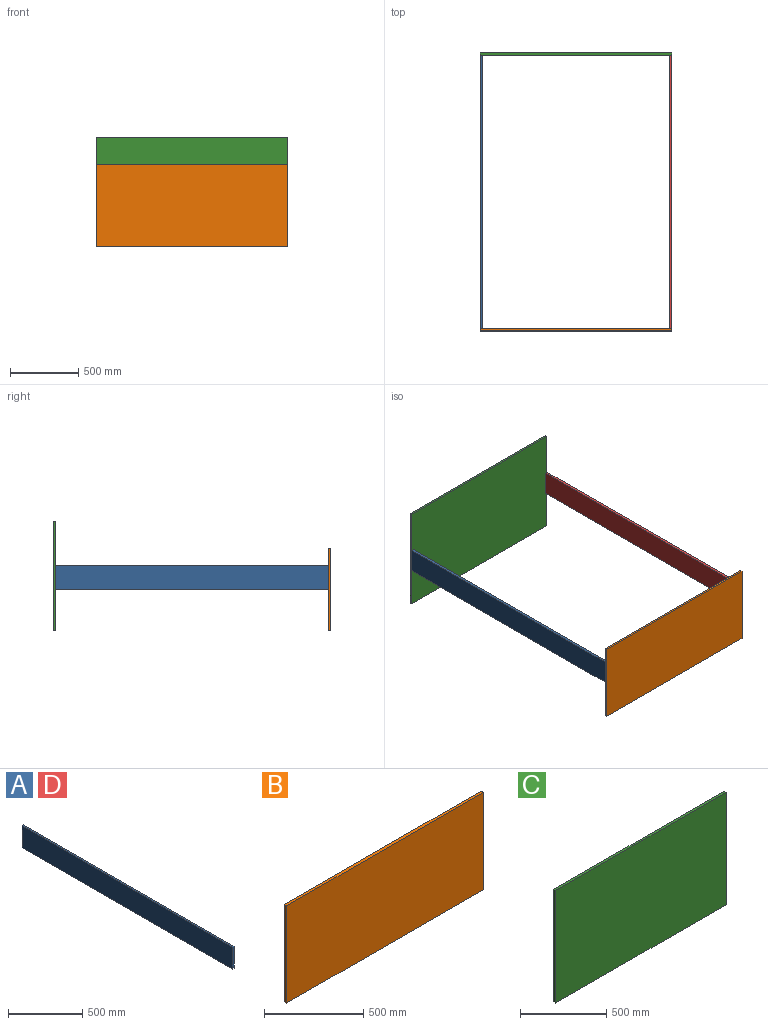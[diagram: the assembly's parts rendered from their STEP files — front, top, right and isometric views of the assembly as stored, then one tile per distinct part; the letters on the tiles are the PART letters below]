
ASSEMBLY  parts=4 mates=3
PART A: 6 faces, bbox 16x2000x180 mm
  f0: plane 2000x16mm, normal (0,0,1), area 32000mm2, adj f1,f3,f4,f5
  f1: plane 180x16mm, normal (0,-1,0), area 2880mm2, adj f0,f2,f4,f5
  f2: plane 2000x16mm, normal (0,0,-1), area 32000mm2, adj f1,f3,f4,f5
  f3: plane 180x16mm, normal (0,1,0), area 2880mm2, adj f0,f2,f4,f5
  f4: plane 2000x180mm, normal (1,0,0), area 360000mm2, adj f0,f1,f2,f3
  f5: plane 2000x180mm, normal (-1,0,0), area 360000mm2, adj f0,f1,f2,f3
PART B: 6 faces, bbox 1400x16x600 mm
  f0: plane 600x16mm, normal (1,0,0), area 9600mm2, adj f1,f3,f4,f5
  f1: plane 1400x16mm, normal (0,0,1), area 22400mm2, adj f0,f2,f4,f5
  f2: plane 600x16mm, normal (-1,0,0), area 9600mm2, adj f1,f3,f4,f5
  f3: plane 1400x16mm, normal (0,0,-1), area 22400mm2, adj f0,f2,f4,f5
  f4: plane 1400x600mm, normal (0,-1,0), area 840000mm2, adj f0,f1,f2,f3
  f5: plane 1400x600mm, normal (0,1,0), area 840000mm2, adj f0,f1,f2,f3
PART C: 6 faces, bbox 1400x16x800 mm
  f0: plane 800x16mm, normal (1,0,0), area 12800mm2, adj f1,f3,f4,f5
  f1: plane 1400x16mm, normal (0,0,1), area 22400mm2, adj f0,f2,f4,f5
  f2: plane 800x16mm, normal (-1,0,0), area 12800mm2, adj f1,f3,f4,f5
  f3: plane 1400x16mm, normal (0,0,-1), area 22400mm2, adj f0,f2,f4,f5
  f4: plane 1400x800mm, normal (0,-1,0), area 1120000mm2, adj f0,f1,f2,f3
  f5: plane 1400x800mm, normal (0,1,0), area 1120000mm2, adj f0,f1,f2,f3
PART D: same geometry as A
PLACE A t=(-631.48,-791.2,255.87)mm
PLACE B t=(68.52,-1791.2,165.87)mm
PLACE C t=(68.52,224.8,265.87)mm
PLACE D t=(752.52,-791.2,255.87)mm
MATE fastened A.f3 <-> C.f4  axis (0,1,0) through (-631.48,208.8,165.87)mm
MATE fastened A.f1 <-> B.f5  axis (0,-1,0) through (-631.48,-1791.2,165.87)mm
MATE fastened D.f3 <-> C.f4  axis (0,1,0) through (768.52,208.8,165.87)mm
